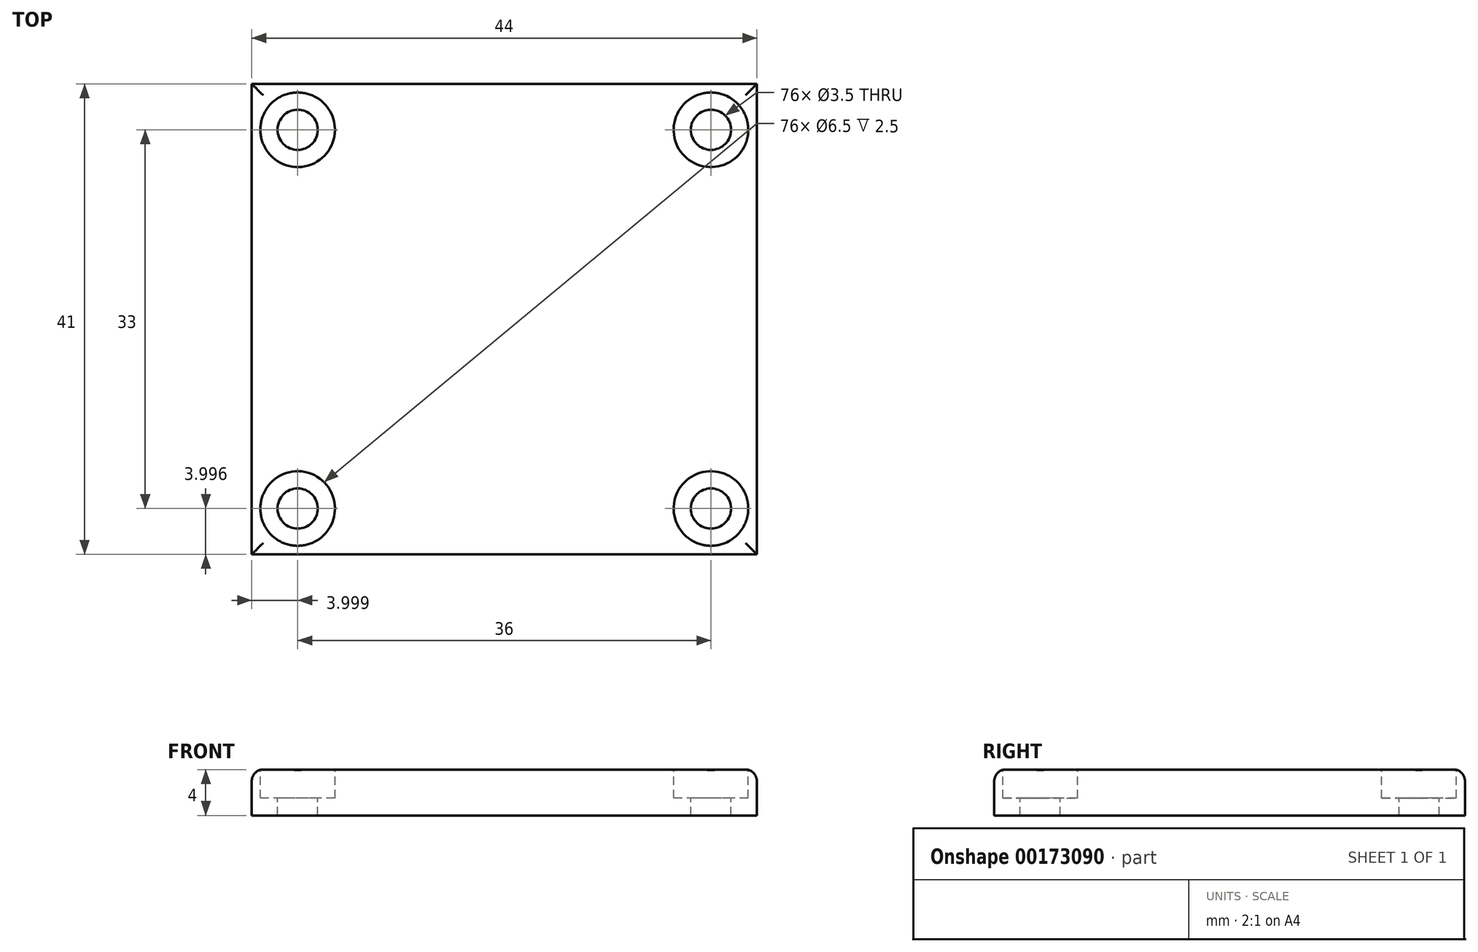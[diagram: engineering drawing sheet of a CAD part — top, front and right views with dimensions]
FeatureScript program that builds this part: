
annotation { "Feature Type Name" : "Feature", "Feature Type Description" : "" }
export const myFeature = defineFeature(function(context is Context, id is Id, definition is map)
    precondition{}
    {
        {
            var Q0;
            Q0=qCreatedBy(makeId("Top.planeOp"),FACE);
            var sketch = newSketch(context, id + "F0", { "sketchPlane" : qUnion([Q0])});
            skLineSegment(sketch, "E0.bottom", {"start": v(-4.04, 1.95) * mm, "end": v(39.96, 1.95) * mm});
            skLineSegment(sketch, "E0.top", {"start": v(-4.04, -39.05) * mm, "end": v(39.96, -39.05) * mm});
            skLineSegment(sketch, "E0.left", {"start": v(-4.04, 1.95) * mm, "end": v(-4.04, -39.05) * mm});
            skLineSegment(sketch, "E0.right", {"start": v(39.96, 1.95) * mm, "end": v(39.96, -39.05) * mm});
            skSolve(sketch);
        }
        {
            var Q0;
            Q0 = qSketchRegion(id + "F0", true);
            extrude(context, id + "F1", {"entities" : qUnion([Q0]), "depth" : 4 * mm});
        }
        {
            var Q0;
            Q0=makeQuery(id+"F1.opExtrude","CAP_FACE",FACE,{"disambiguationData":[OSD([sQuery(id+"F0.wireOp",EDGE,"E0.bottom"),sQuery(id+"F0.wireOp",EDGE,"E0.top"),sQuery(id+"F0.wireOp",EDGE,"E0.left"),sQuery(id+"F0.wireOp",EDGE,"E0.right")])],"isStart":false});
            var sketch = newSketch(context, id + "F2", { "sketchPlane" : qUnion([Q0])});
            skLineSegment(sketch, "E1.0", {"start": v(-0.04, -2.05) * mm, "end": v(35.96, -2.05) * mm, "construction": true});
            skLineSegment(sketch, "E1.1", {"start": v(-0.04, -2.05) * mm, "end": v(-0.04, -35.05) * mm, "construction": true});
            skLineSegment(sketch, "E1.2", {"start": v(-0.04, -35.05) * mm, "end": v(35.96, -35.05) * mm, "construction": true});
            skLineSegment(sketch, "E1.3", {"start": v(35.96, -2.05) * mm, "end": v(35.96, -35.05) * mm, "construction": true});
            skCircle(sketch, "E2", {"center": v(-0.04, -2.05) * mm, "radius": 1.75 * mm});
            skCircle(sketch, "E3", {"center": v(35.96, -2.05) * mm, "radius": 1.75 * mm});
            skCircle(sketch, "E4", {"center": v(35.96, -35.05) * mm, "radius": 1.75 * mm});
            skCircle(sketch, "E5", {"center": v(-0.04, -35.05) * mm, "radius": 1.75 * mm});
            skSolve(sketch);
        }
        {
            var Q0;
            Q0 = qSketchRegion(id + "F2", true);
            extrude(context, id + "F3", {"entities" : qUnion([Q0]), "operationType" : NewBodyOperationType.REMOVE, "endBound" : BoundingType.THROUGH_ALL, "oppositeDirection" : true, "depth" : 25 * mm});
        }
        {
            var Q0;
            Q0=makeQuery(id+"F1.opExtrude","CAP_FACE",FACE,{"disambiguationData":[OSD([sQuery(id+"F0.wireOp",EDGE,"E0.bottom"),sQuery(id+"F0.wireOp",EDGE,"E0.top"),sQuery(id+"F0.wireOp",EDGE,"E0.left"),sQuery(id+"F0.wireOp",EDGE,"E0.right")])],"isStart":false});
            var sketch = newSketch(context, id + "F4", { "sketchPlane" : qUnion([Q0])});
            skCircle(sketch, "E6", {"center": v(-0.04, -2.05) * mm, "radius": 3.25 * mm});
            skCircle(sketch, "E7", {"center": v(35.96, -2.05) * mm, "radius": 3.25 * mm});
            skCircle(sketch, "E8", {"center": v(35.96, -35.05) * mm, "radius": 3.25 * mm});
            skCircle(sketch, "E9", {"center": v(-0.04, -35.05) * mm, "radius": 3.25 * mm});
            skSolve(sketch);
        }
        {
            var Q0;
            Q0 = qSketchRegion(id + "F4", true);
            extrude(context, id + "F5", {"entities" : qUnion([Q0]), "operationType" : NewBodyOperationType.REMOVE, "oppositeDirection" : true, "depth" : 2.5 * mm});
        }
        {
            var Q0;
            Q0=makeQuery(id+"F1.opExtrude","CAP_EDGE",EDGE,{"disambiguationData":[OSD([sQuery(id+"F0.wireOp",EDGE,"E0.left")])],"isStart":false});
            var Q1;
            Q1=makeQuery(id+"F1.opExtrude","CAP_EDGE",EDGE,{"disambiguationData":[OSD([sQuery(id+"F0.wireOp",EDGE,"E0.top")])],"isStart":false});
            var Q2;
            Q2=makeQuery(id+"F1.opExtrude","CAP_EDGE",EDGE,{"disambiguationData":[OSD([sQuery(id+"F0.wireOp",EDGE,"E0.right")])],"isStart":false});
            var Q3;
            Q3=makeQuery(id+"F1.opExtrude","CAP_EDGE",EDGE,{"disambiguationData":[OSD([sQuery(id+"F0.wireOp",EDGE,"E0.bottom")])],"isStart":false});
            fillet(context, id + "F6", {"entities" : qUnion([Q0, Q1, Q2, Q3]), "radius" : 1 * mm, "tangentPropagation" : true, "allowEdgeOverflow" : false});
        }
    });
